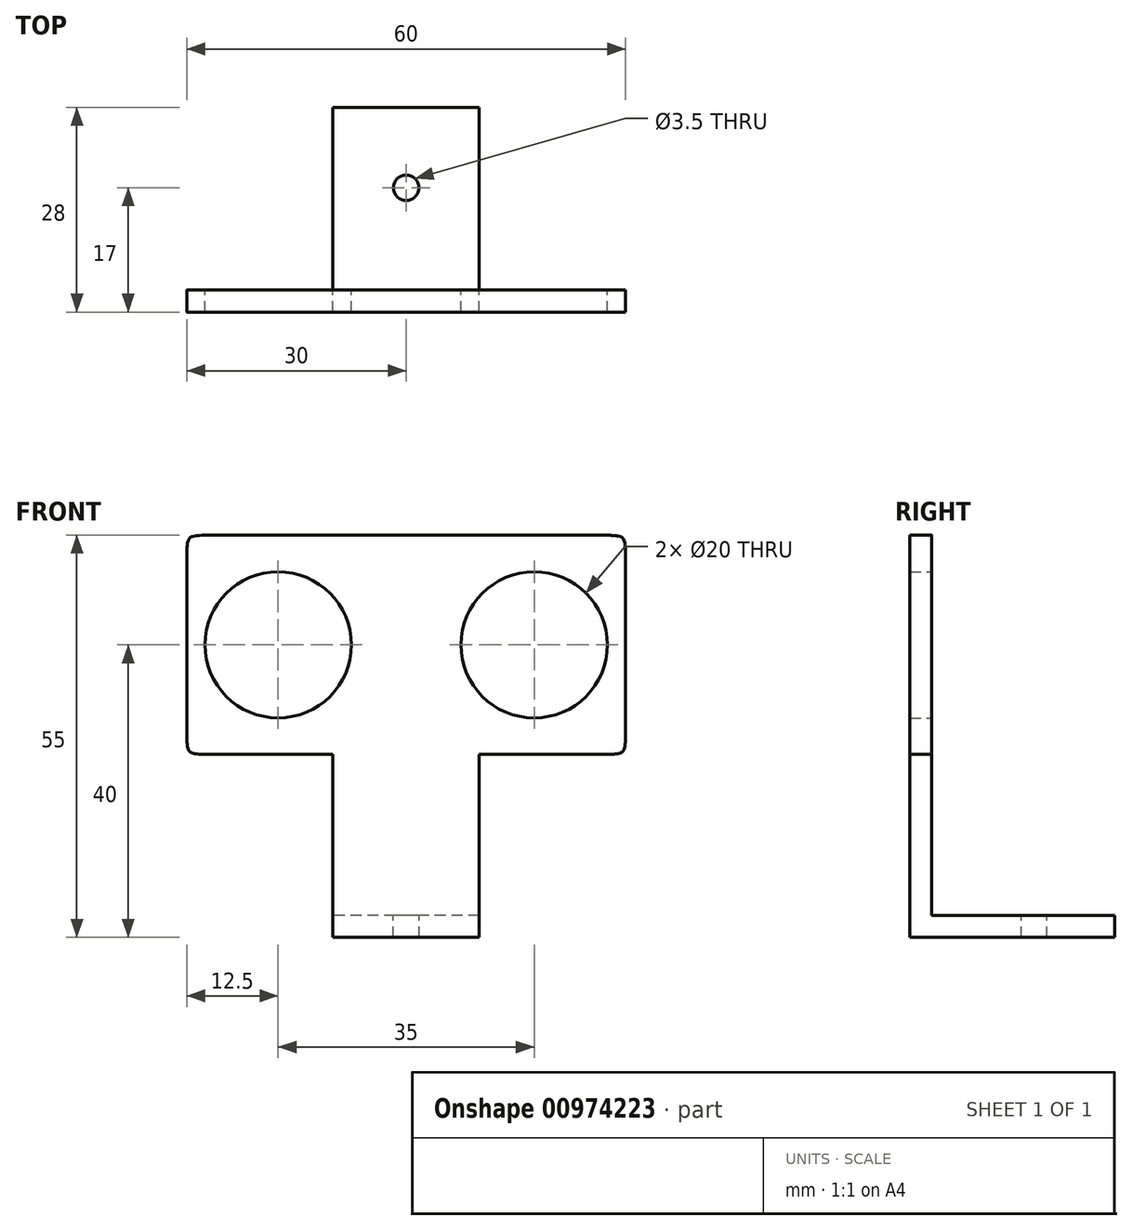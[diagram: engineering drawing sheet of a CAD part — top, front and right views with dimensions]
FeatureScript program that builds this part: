
annotation { "Feature Type Name" : "Feature", "Feature Type Description" : "" }
export const myFeature = defineFeature(function(context is Context, id is Id, definition is map)
    precondition{}
    {
        {
            var Q0;
            Q0=qCreatedBy(makeId("Front.planeOp"),FACE);
            var sketch = newSketch(context, id + "F0", { "sketchPlane" : qUnion([Q0])});
            skLineSegment(sketch, "E0.bottom", {"start": v(30, 15) * mm, "end": v(-30, 15) * mm});
            skLineSegment(sketch, "E0.top", {"start": v(30, -15) * mm, "end": v(-30, -15) * mm});
            skLineSegment(sketch, "E0.left", {"start": v(30, 15) * mm, "end": v(30, -15) * mm});
            skLineSegment(sketch, "E0.right", {"start": v(-30, 15) * mm, "end": v(-30, -15) * mm});
            skPoint(sketch, "E0.middle", {"position": v(0, 0) * mm});
            skLineSegment(sketch, "E1", {"start": v(-17.5, 0) * mm, "end": v(17.5, 0) * mm});
            skCircle(sketch, "E2", {"center": v(-17.5, 0) * mm, "radius": 10 * mm});
            skCircle(sketch, "E3", {"center": v(17.5, 0) * mm, "radius": 10 * mm});
            skSolve(sketch);
        }
        {
            var Q0;
            Q0 = qSketchRegion(id + "F0", true);
            extrude(context, id + "F1", {"entities" : qUnion([Q0]), "depth" : 3 * mm, "offsetDistance" : 25 * mm});
        }
        {
            var Q0;
            Q0=makeQuery(id+"F1.opExtrude","SWEPT_EDGE",EDGE,{"disambiguationData":[OSD([sQuery(id+"F0.wireOp",EDGE,"E0.top"),sQuery(id+"F0.wireOp",EDGE,"E0.left")])]});
            var Q1;
            Q1=makeQuery(id+"F1.opExtrude","SWEPT_EDGE",EDGE,{"disambiguationData":[OSD([sQuery(id+"F0.wireOp",EDGE,"E0.top"),sQuery(id+"F0.wireOp",EDGE,"E0.right")])]});
            var Q2;
            Q2=makeQuery(id+"F1.opExtrude","SWEPT_EDGE",EDGE,{"disambiguationData":[OSD([sQuery(id+"F0.wireOp",EDGE,"E0.bottom"),sQuery(id+"F0.wireOp",EDGE,"E0.left")])]});
            var Q3;
            Q3=makeQuery(id+"F1.opExtrude","SWEPT_EDGE",EDGE,{"disambiguationData":[OSD([sQuery(id+"F0.wireOp",EDGE,"E0.bottom"),sQuery(id+"F0.wireOp",EDGE,"E0.right")])]});
            fillet(context, id + "F2", {"entities" : qUnion([Q0, Q1, Q2, Q3]), "radius" : 4 * mm, "tangentPropagation" : true, "rho" : 0.8, "crossSection" : FilletCrossSection.CONIC, "allowEdgeOverflow" : false});
        }
        {
            var Q0;
            Q0=makeQuery(id+"F1.opExtrude","SWEPT_FACE",FACE,{"disambiguationData":[OSD([sQuery(id+"F0.wireOp",EDGE,"E0.top")])]});
            var sketch = newSketch(context, id + "F3", { "sketchPlane" : qUnion([Q0])});
            skLineSegment(sketch, "E4.bottom", {"start": v(10, 3) * mm, "end": v(-10, 3) * mm});
            skLineSegment(sketch, "E4.top", {"start": v(10, 0) * mm, "end": v(-10, 0) * mm});
            skLineSegment(sketch, "E4.left", {"start": v(10, 3) * mm, "end": v(10, 0) * mm});
            skLineSegment(sketch, "E4.right", {"start": v(-10, 3) * mm, "end": v(-10, 0) * mm});
            skLineSegment(sketch, "E5", {"start": v(0, 10.9) * mm, "end": v(0, 3) * mm, "construction": true});
            skSolve(sketch);
        }
        {
            var Q0;
            Q0 = qSketchRegion(id + "F3", true);
            extrude(context, id + "F4", {"entities" : qUnion([Q0]), "operationType" : NewBodyOperationType.ADD, "depth" : 25 * mm, "offsetDistance" : 25 * mm});
        }
        {
            var Q0;
            Q0=makeQuery(id+"F4.boolean.opBoolean","MERGE",FACE,{"derivedFrom":[makeQuery(id+"F1.opExtrude","CAP_FACE",FACE,{"disambiguationData":[OSD([sQuery(id+"F0.wireOp",EDGE,"E0.bottom"),sQuery(id+"F0.wireOp",EDGE,"E0.top"),sQuery(id+"F0.wireOp",EDGE,"E0.left"),sQuery(id+"F0.wireOp",EDGE,"E0.right"),sQuery(id+"F0.wireOp",EDGE,"E2"),sQuery(id+"F0.wireOp",EDGE,"E3")])],"isStart":true}),makeQuery(id+"F4.opExtrude","SWEPT_FACE",FACE,{"disambiguationData":[OSD([sQuery(id+"F3.wireOp",EDGE,"E4.top")])]})]});
            var sketch = newSketch(context, id + "F5", { "sketchPlane" : qUnion([Q0])});
            skLineSegment(sketch, "E6.bottom", {"start": v(-10, -40) * mm, "end": v(10, -40) * mm});
            skLineSegment(sketch, "E6.top", {"start": v(-10, -37) * mm, "end": v(10, -37) * mm});
            skLineSegment(sketch, "E6.left", {"start": v(-10, -40) * mm, "end": v(-10, -37) * mm});
            skLineSegment(sketch, "E6.right", {"start": v(10, -40) * mm, "end": v(10, -37) * mm});
            skSolve(sketch);
        }
        {
            var Q0;
            Q0 = qSketchRegion(id + "F5", true);
            extrude(context, id + "F6", {"entities" : qUnion([Q0]), "operationType" : NewBodyOperationType.ADD, "depth" : 25 * mm, "offsetDistance" : 25 * mm});
        }
        {
            var Q0;
            Q0=makeQuery(id+"F6.opExtrude","SWEPT_FACE",FACE,{"disambiguationData":[OSD([sQuery(id+"F5.wireOp",EDGE,"E6.top")])]});
            var sketch = newSketch(context, id + "F7", { "sketchPlane" : qUnion([Q0])});
            skCircle(sketch, "E7", {"center": v(0, 14) * mm, "radius": 1.75 * mm});
            skLineSegment(sketch, "E8", {"start": v(0, 0) * mm, "end": v(0, 14) * mm, "construction": true});
            skSolve(sketch);
        }
        {
            var Q0;
            Q0 = qSketchRegion(id + "F7", true);
            extrude(context, id + "F8", {"entities" : qUnion([Q0]), "operationType" : NewBodyOperationType.REMOVE, "endBound" : BoundingType.THROUGH_ALL, "oppositeDirection" : true, "depth" : 25 * mm, "offsetDistance" : 25 * mm});
        }
    });
